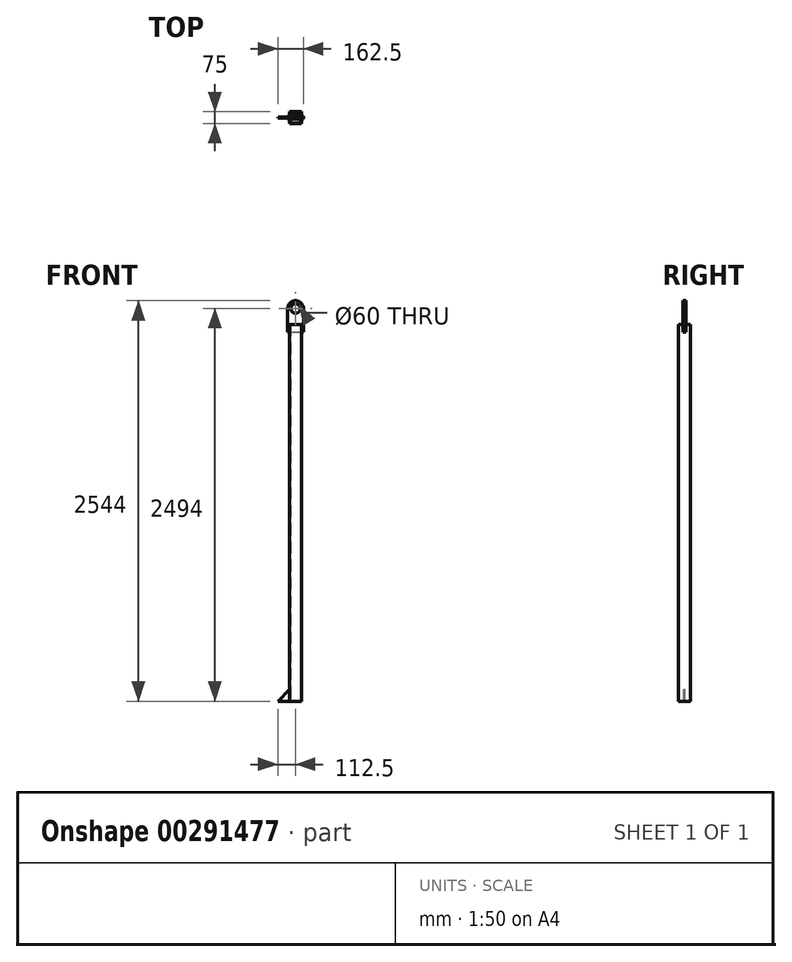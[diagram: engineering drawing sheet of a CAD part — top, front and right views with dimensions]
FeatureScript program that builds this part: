
annotation { "Feature Type Name" : "Feature", "Feature Type Description" : "" }
export const myFeature = defineFeature(function(context is Context, id is Id, definition is map)
    precondition{}
    {
        {
            var Q0;
            Q0=qCreatedBy(makeId("Top.planeOp"),FACE);
            var sketch = newSketch(context, id + "F0", { "sketchPlane" : qUnion([Q0])});
            skLineSegment(sketch, "E0.bottom", {"start": v(37.5, 37.5) * mm, "end": v(-37.5, 37.5) * mm});
            skLineSegment(sketch, "E0.top", {"start": v(37.5, -37.5) * mm, "end": v(-37.5, -37.5) * mm});
            skLineSegment(sketch, "E0.left", {"start": v(37.5, 37.5) * mm, "end": v(37.5, -37.5) * mm});
            skLineSegment(sketch, "E0.right", {"start": v(-37.5, 37.5) * mm, "end": v(-37.5, -37.5) * mm});
            skPoint(sketch, "E0.middle", {"position": v(0, 0) * mm});
            skLineSegment(sketch, "E1.0", {"start": v(33, 33) * mm, "end": v(-33, 33) * mm});
            skLineSegment(sketch, "E2.0", {"start": v(-33, 33) * mm, "end": v(-33, -33) * mm});
            skLineSegment(sketch, "E3.0", {"start": v(33, -33) * mm, "end": v(-33, -33) * mm});
            skLineSegment(sketch, "E4.0", {"start": v(33, 33) * mm, "end": v(33, -33) * mm});
            skSolve(sketch);
        }
        {
            var Q0;
            Q0 = qSketchRegion(id + "F0", true);
            extrude(context, id + "F1", {"entities" : qUnion([Q0]), "depth" : 2394 * mm});
        }
        {
            var Q0;
            Q0=qCreatedBy(makeId("Front.planeOp"),FACE);
            var sketch = newSketch(context, id + "F2", { "sketchPlane" : qUnion([Q0])});
            skLineSegment(sketch, "E5.bottom", {"start": v(-50, 2344) * mm, "end": v(50, 2344) * mm});
            skLineSegment(sketch, "E5.left", {"start": v(-50, 2344) * mm, "end": v(-50, 2494) * mm});
            skLineSegment(sketch, "E5.right", {"start": v(50, 2344) * mm, "end": v(50, 2494) * mm});
            skPoint(sketch, "E6.firstSnap0", {"position": v(0, 2344) * mm});
            skCircle(sketch, "E7", {"center": v(0, 2494) * mm, "radius": 30 * mm});
            skArc(sketch, "E8", {"start": v(50, 2494) * mm, "mid": v(0, 2544) * mm, "end": v(-50, 2494) * mm});
            skSolve(sketch);
        }
        {
            var Q0;
            Q0 = qSketchRegion(id + "F2", true);
            extrude(context, id + "F3", {"entities" : qUnion([Q0]), "operationType" : NewBodyOperationType.ADD, "endBound" : BoundingType.SYMMETRIC, "depth" : 19 * mm});
        }
        {
            var Q0;
            Q0=qCreatedBy(makeId("Front.planeOp"),FACE);
            var sketch = newSketch(context, id + "F4", { "sketchPlane" : qUnion([Q0])});
            skLineSegment(sketch, "E9", {"start": v(-37.5, 0) * mm, "end": v(-37.5, 75) * mm});
            skLineSegment(sketch, "E10", {"start": v(-37.5, 75) * mm, "end": v(-112.5, 0) * mm});
            skLineSegment(sketch, "E11", {"start": v(-112.5, 0) * mm, "end": v(-37.5, 0) * mm});
            skSolve(sketch);
        }
        {
            var Q0;
            Q0 = qSketchRegion(id + "F4", true);
            extrude(context, id + "F5", {"entities" : qUnion([Q0]), "operationType" : NewBodyOperationType.ADD, "endBound" : BoundingType.SYMMETRIC, "depth" : 6 * mm});
        }
    });
